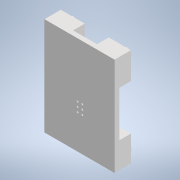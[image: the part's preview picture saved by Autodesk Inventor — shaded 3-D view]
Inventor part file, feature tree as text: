
AUTODESK INVENTOR PART (.ipt)
format: ipt  version: 2022 (Build 260153000, 153)  size: 203,776 bytes
history: native  units: in
note: dims shown in document units (in); Inventor stores cm internally (conversion verified against a paired STEP export)
features: reference x40, extrude x6, sketch x6, other x4, plane x1
ambient origin geometry x8: Origin, YZ Plane, XZ Plane, XY Plane, X Axis, Y Axis, Z Axis, Center Point
bodies: Solid1 (feature_tree)
feature tree (57):
  extrude  "Extrusion1"  Depth=0.0197in
  extrude  "Extrusion2"  Depth=0.0197in
  extrude  "Extrusion3"  Depth=0.0197in
  plane  "Work Plane1"
  extrude  "Extrusion4"  Depth=0.0197in
  extrude  "Extrusion5"  Depth=0.0197in
  extrude  "Extrusion6"  Depth=0.0197in
  sketch  "Sketch1"  dims[d0=0.1in d1=0.0in d2=0.0197in]
  reference  "Reference1"
  reference  "Reference2"
  reference  "Reference3"
  reference  "Reference4"
  reference  "Reference5"
  reference  "Reference6"
  reference  "Reference7"
  reference  "Reference8"
  sketch  "Sketch2"  dims[d3=0.0197in d4=0.0197in]
  reference  "Reference9"
  reference  "Reference10"
  reference  "Reference11"
  reference  "Reference12"
  reference  "Reference13"
  reference  "Reference14"
  reference  "Reference15"
  reference  "Reference16"
  reference  "Reference17"
  reference  "Reference18"
  reference  "Reference19"
  reference  "Reference20"
  reference  "Reference21"
  reference  "Reference22"
  reference  "Reference23"
  reference  "Reference24"
  reference  "Reference25"
  reference  "Reference26"
  reference  "Reference27"
  reference  "Reference28"
  sketch  "Sketch3"  dims[d5=0.0197in d6=0.0197in]
  sketch  "Sketch4"  dims[d7=0.0197in d8=0.0197in]
  reference  "Reference29"
  reference  "Reference30"
  sketch  "Sketch5"  dims[d9=0.0197in d10=0.0197in]
  reference  "Reference31"
  reference  "Reference32"
  reference  "Reference33"
  reference  "Reference34"
  reference  "Reference35"
  reference  "Reference36"
  sketch  "Sketch6"  dims[d11=0.0197in d12=0.0197in d13=0.0197in d14=0.0197in d15=0.0197in d16=0.25in d17=0.0in d18=1.118in d19=0.5086in d20=0.04in d21=0.25in d22=0.0in d23=0.02in d24=0.16in d25=0.0in d26=0.0in d27=0.0in d28=0.165in d29=0.1in d30=0.0in]
  reference  "Reference37"
  reference  "Reference38"
  reference  "Reference39"
  reference  "Reference40"
  other  "Assembly2"
  other  "board:1"
  other  "Male_Pin_1x3:2"
  other  "Male_Pin_1x3:1"
